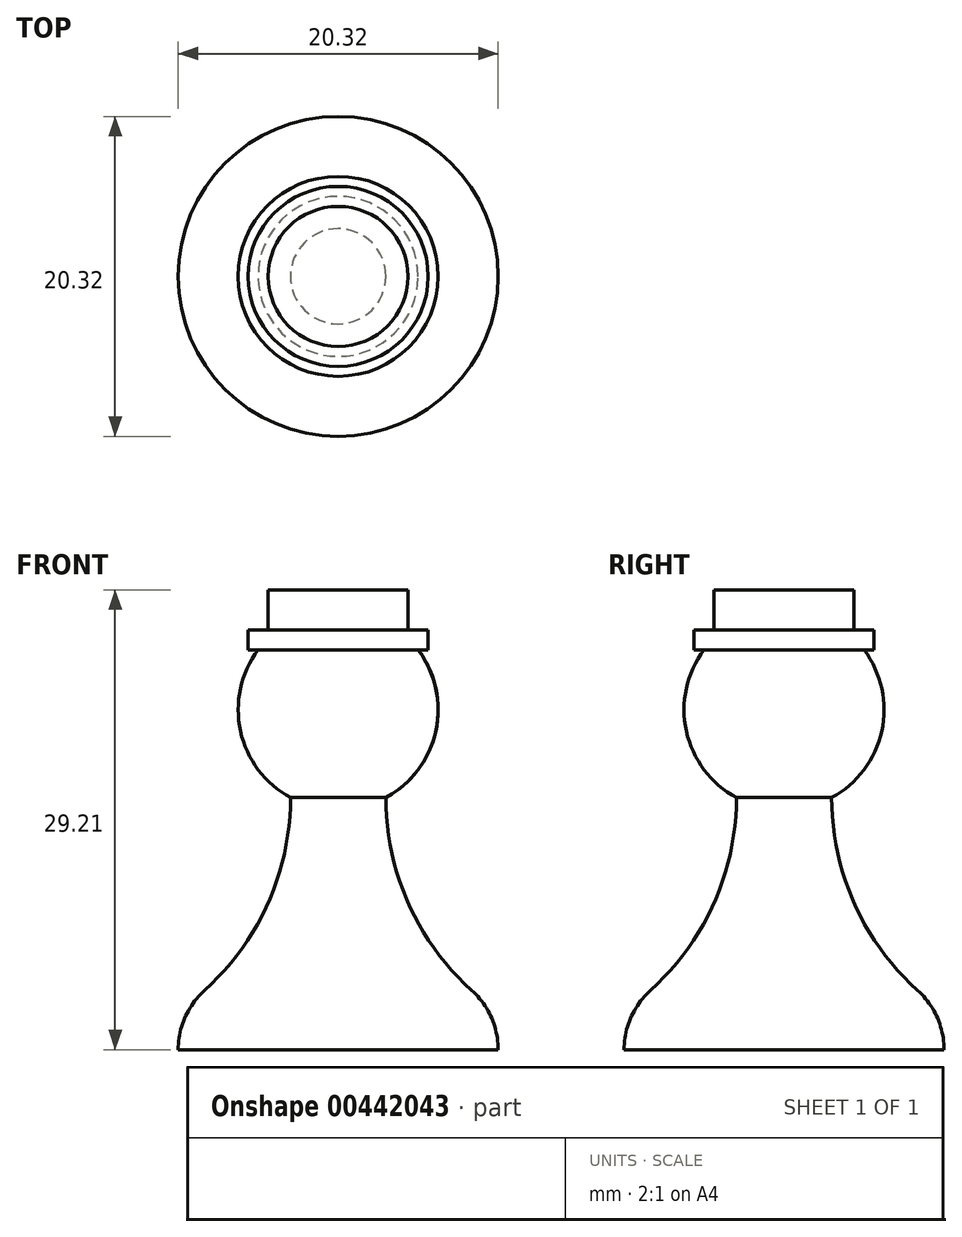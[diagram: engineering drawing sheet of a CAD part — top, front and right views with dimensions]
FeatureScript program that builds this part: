
annotation { "Feature Type Name" : "Feature", "Feature Type Description" : "" }
export const myFeature = defineFeature(function(context is Context, id is Id, definition is map)
    precondition{}
    {
        {
            var Q0;
            Q0=qCreatedBy(makeId("Front.planeOp"),FACE);
            var sketch = newSketch(context, id + "F0", { "sketchPlane" : qUnion([Q0])});
            skArc(sketch, "E0", {"start": v(0, 27.94) * mm, "mid": v(-6.35, 21.6) * mm, "end": v(0, 15.24) * mm});
            skLineSegment(sketch, "E1", {"start": v(0, 0) * mm, "end": v(-10.16, 0) * mm});
            skArc(sketch, "E2", {"start": v(-8.48, 3.77) * mm, "mid": v(-9.72, 2.07) * mm, "end": v(-10.16, 0) * mm});
            skArc(sketch, "E3", {"start": v(-8.48, 3.77) * mm, "mid": v(-4.45, 9.31) * mm, "end": v(-3.02, 16) * mm});
            skLineSegment(sketch, "E4", {"start": v(-3.02, 16) * mm, "end": v(-3.02, 0) * mm, "construction": true});
            skLineSegment(sketch, "E5", {"start": v(0, 27.94) * mm, "end": v(0, 0) * mm});
            skLineSegment(sketch, "E6", {"start": v(-10.16, 0) * mm, "end": v(-10.16, 3.2) * mm, "construction": true});
            skSolve(sketch);
        }
        {
            var Q0;
            Q0=qSketchRegion(id+"F0",true);
            var Q1;
            Q1=sQuery(id+"F0.wireOp",EDGE,"E5");
            revolve(context, id + "F1", {"entities" : qUnion([Q0]), "axis" : qUnion([Q1]), "revolveType" : RevolveType.FULL});
        }
        {
            var Q0;
            Q0=qCreatedBy(makeId("Top.planeOp"),FACE);
            cPlane(context, id + "F2", {"entities" : qUnion([Q0]), "cplaneType" : CPlaneType.OFFSET, "offset" : 25.4 * mm, "width" : 152.4 * mm, "height" : 152.4 * mm});
        }
        {
            var Q0;
            Q0=qCreatedBy(id+"F2.planeOp",FACE);
            var sketch = newSketch(context, id + "F3", { "sketchPlane" : qUnion([Q0])});
            skCircle(sketch, "E7", {"center": v(0, 0) * mm, "radius": 5.72 * mm});
            skCircle(sketch, "E8", {"center": v(0, 0) * mm, "radius": 4.45 * mm});
            skSolve(sketch);
        }
        {
            var Q0;
            Q0=makeQuery(id+"F3.imprint","IMPRINT",FACE,{"disambiguationData":[TD([[makeQuery(id+"F3.imprint","IMPRINT",EDGE,{"derivedFrom":sQuery(id+"F3.wireOp",EDGE,"E7")}),1.0]])]});
            extrude(context, id + "F4", {"entities" : qUnion([Q0]), "operationType" : NewBodyOperationType.ADD, "depth" : 1.27 * mm});
        }
        {
            var Q0;
            Q0=makeQuery(id+"F3.imprint","IMPRINT",FACE,{"disambiguationData":[TD([[makeQuery(id+"F3.imprint","IMPRINT",EDGE,{"derivedFrom":sQuery(id+"F3.wireOp",EDGE,"E8")}),1.0]])]});
            var Q1;
            Q1=sQuery(id+"F3.wireOp",EDGE,"E8");
            extrude(context, id + "F5", {"entities" : qUnion([Q0]), "operationType" : NewBodyOperationType.ADD, "surfaceEntities" : qUnion([Q1]), "depth" : 3.8 * mm});
        }
    });
